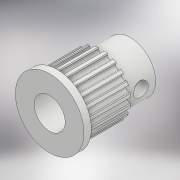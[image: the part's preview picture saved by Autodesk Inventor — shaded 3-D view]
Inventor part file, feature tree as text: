
AUTODESK INVENTOR PART (.ipt)
format: ipt  version: 2018.2 (Build 222227000, 227)  size: 260,608 bytes
history: native  units: mm
features: extrude x6, sketch x5, pattern_circular x1
ambient origin geometry x8: Origin, YZ Plane, XZ Plane, XY Plane, X Axis, Y Axis, Z Axis, Center Point
bodies: Solid1 (feature_tree)
feature tree (12):
  extrude  "Extrusion1"  Depth=0.5mm
  extrude  "Extrusion2"  Depth=7.0mm TaperAngle=0.0deg
  pattern_circular  "Circular Pattern1"  [2 undecoded]
  extrude  "Extrusion3"  Depth=1.0mm TaperAngle=0.0deg
  sketch  "Sketch4"  dims[d18=6.35mm]
  extrude  "Extrusion4"  Depth=6.0mm TaperAngle=0.0deg
  extrude  "Extrusion5"  Depth=3.0mm
  extrude  "Extrusion6"  Depth=6.0mm TaperAngle=0.0deg
  sketch  "Sketch1"  dims[d8=0.0mm d9=0.5mm]
  sketch  "Sketch2"  dims[d10=0.15mm d12=7.0mm d13=0.0mm]
  sketch  "Sketch3"  dims[d15=360.0deg]
  sketch  "Sketch5"  dims[d20=0.0mm d21=2.0mm d22=1.0mm d23=0.0mm d24=6.0mm d25=0.0mm d26=3.0mm d27=6.0mm d28=0.0mm]
note: 2 required parameter values undecoded (feature->parameter linkage not recoverable at this tier; creation-order binding heuristic only, values carry confidence <= 0.55)
